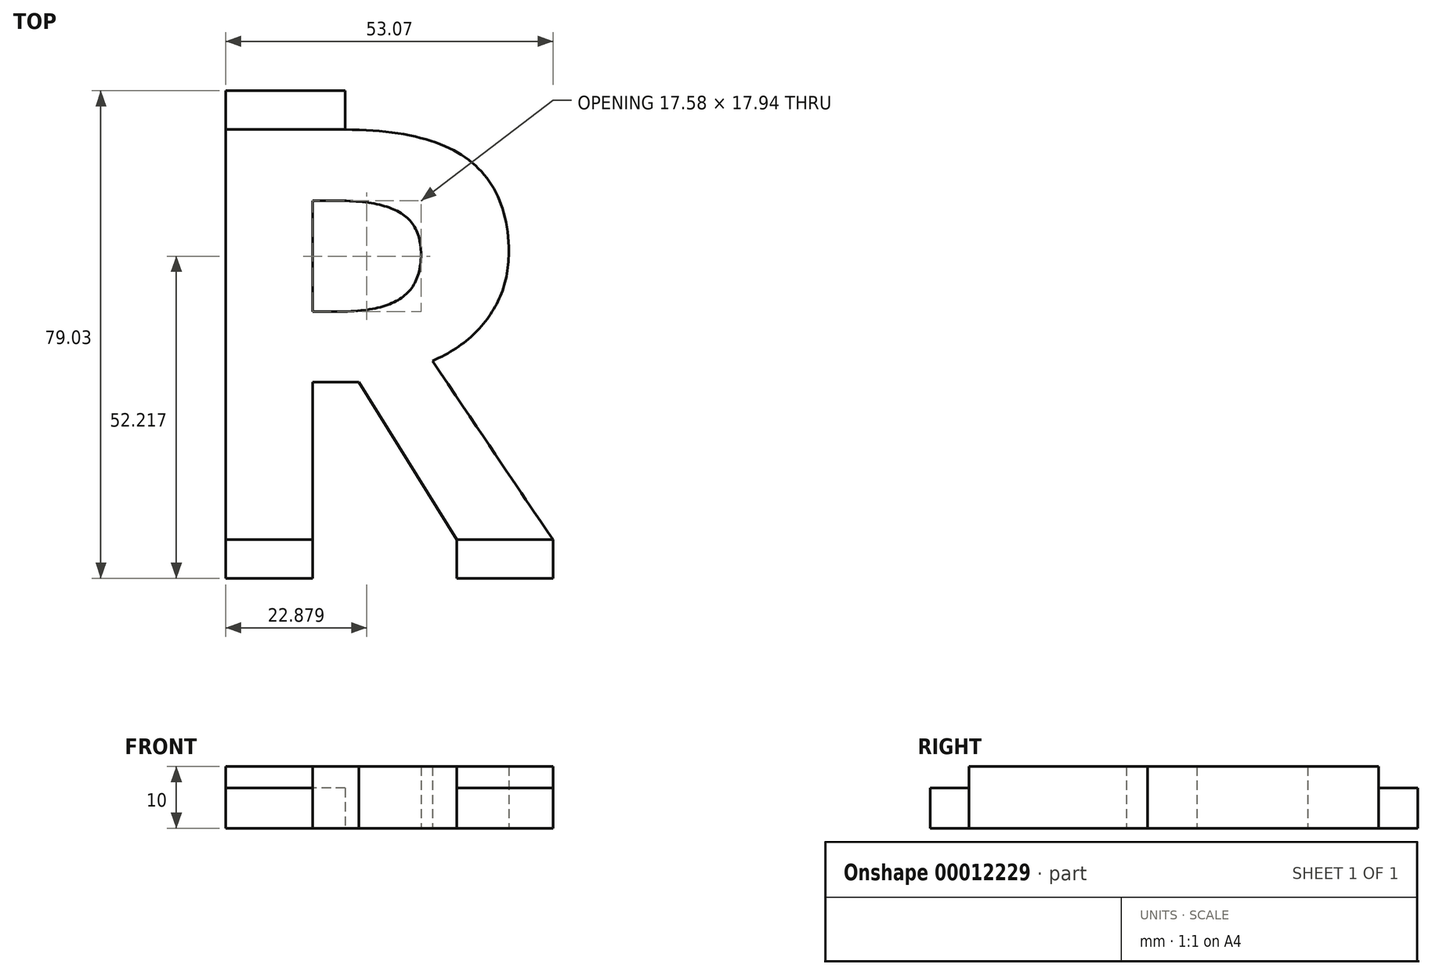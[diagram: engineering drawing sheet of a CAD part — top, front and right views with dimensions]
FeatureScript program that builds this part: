
annotation { "Feature Type Name" : "Feature", "Feature Type Description" : "" }
export const myFeature = defineFeature(function(context is Context, id is Id, definition is map)
    precondition{}
    {
        {
            var Q0;
            Q0=qCreatedBy(makeId("Top.planeOp"),FACE);
            var sketch = newSketch(context, id + "F0", { "sketchPlane" : qUnion([Q0])});
            skText(sketch, "E0", { "text": "R", "fontName": "OpenSans-Bold.ttf"});
            skLineSegment(sketch, "E1", {"start": v(-53.06, 66.47) * mm, "end": v(-5.63, 66.47) * mm, "construction": true});
            const initialGuessF0  = {"E0": [-0.06143, 0, 1, 0, 0.067]};
            skSetInitialGuess(sketch, initialGuessF0);
            skSolve(sketch);
        }
        {
            var Q0;
            Q0=makeQuery(id+"F0.imprint","IMPRINT",FACE,{"disambiguationData":[TD([[makeQuery(id+"F0.imprint","IMPRINT",EDGE,{"derivedFrom":sQuery(id+"F0.wireOp",EDGE,"E0.sketch_text.stroke-0")}),-1.0]])]});
            extrude(context, id + "F1", {"entities" : qUnion([Q0]), "depth" : 10 * mm});
        }
        {
            var Q0;
            Q0=makeQuery(id+"F1.opExtrude","SWEPT_FACE",FACE,{"disambiguationData":[OSD([sQuery(id+"F0.wireOp",EDGE,"E0.sketch_text.stroke-8")])]});
            var sketch = newSketch(context, id + "F2", { "sketchPlane" : qUnion([Q0])});
            skLineSegment(sketch, "E2.0.0", {"start": v(-53.07, 0) * mm, "end": v(-38.98, 0) * mm});
            skLineSegment(sketch, "E2.0.1", {"start": v(-38.98, 0) * mm, "end": v(-38.98, 10) * mm});
            skLineSegment(sketch, "E2.0.2", {"start": v(-38.98, 10) * mm, "end": v(-53.07, 10) * mm});
            skLineSegment(sketch, "E2.0.3", {"start": v(-53.07, 10) * mm, "end": v(-53.07, 0) * mm});
            skLineSegment(sketch, "E3.0.0", {"start": v(-15.63, 0) * mm, "end": v(0, 0) * mm});
            skLineSegment(sketch, "E3.0.1", {"start": v(0, 0) * mm, "end": v(0, 10) * mm});
            skLineSegment(sketch, "E3.0.2", {"start": v(0, 10) * mm, "end": v(-15.63, 10) * mm});
            skLineSegment(sketch, "E3.0.3", {"start": v(-15.63, 10) * mm, "end": v(-15.63, 0) * mm});
            skLineSegment(sketch, "E4.top", {"start": v(-53.07, 6.5) * mm, "end": v(-38.98, 6.5) * mm});
            skLineSegment(sketch, "E4.left", {"start": v(-53.07, 0) * mm, "end": v(-53.07, 6.5) * mm});
            skLineSegment(sketch, "E4.right", {"start": v(-38.98, 0) * mm, "end": v(-38.98, 6.5) * mm});
            skLineSegment(sketch, "E5.top", {"start": v(-15.63, 6.5) * mm, "end": v(0, 6.5) * mm});
            skLineSegment(sketch, "E5.left", {"start": v(-15.63, 0) * mm, "end": v(-15.63, 6.5) * mm});
            skLineSegment(sketch, "E5.right", {"start": v(0, 0) * mm, "end": v(0, 6.5) * mm});
            skSolve(sketch);
        }
        {
            var Q0;
            Q0=makeQuery(id+"F2.imprint","IMPRINT",FACE,{"disambiguationData":[TD([[makeQuery(id+"F2.imprint","IMPRINT",EDGE,{"derivedFrom":sQuery(id+"F2.wireOp",EDGE,"E2.0.0")}),-1.0]])]});
            var Q1;
            Q1=makeQuery(id+"F2.imprint","IMPRINT",FACE,{"disambiguationData":[TD([[makeQuery(id+"F2.imprint","IMPRINT",EDGE,{"derivedFrom":sQuery(id+"F2.wireOp",EDGE,"E3.0.0")}),1.0]])]});
            extrude(context, id + "F3", {"entities" : qUnion([Q0, Q1]), "operationType" : NewBodyOperationType.ADD, "depth" : 6.3 * mm});
        }
        {
            var Q0;
            Q0=makeQuery(id+"F1.opExtrude","SWEPT_FACE",FACE,{"disambiguationData":[OSD([sQuery(id+"F0.wireOp",EDGE,"E0.sketch_text.stroke-10")])]});
            var sketch = newSketch(context, id + "F4", { "sketchPlane" : qUnion([Q0])});
            skLineSegment(sketch, "E6.0.0", {"start": v(33.72, 0) * mm, "end": v(53.07, 0) * mm});
            skLineSegment(sketch, "E6.0.1", {"start": v(53.07, 0) * mm, "end": v(53.07, 10) * mm});
            skLineSegment(sketch, "E6.0.2", {"start": v(53.07, 10) * mm, "end": v(33.72, 10) * mm});
            skLineSegment(sketch, "E6.0.3", {"start": v(33.72, 10) * mm, "end": v(33.72, 0) * mm});
            skLineSegment(sketch, "E7.top", {"start": v(33.72, 6.5) * mm, "end": v(53.07, 6.5) * mm});
            skLineSegment(sketch, "E7.left", {"start": v(33.72, 0) * mm, "end": v(33.72, 6.5) * mm});
            skLineSegment(sketch, "E7.right", {"start": v(53.07, 0) * mm, "end": v(53.07, 6.5) * mm});
            skSolve(sketch);
        }
        {
            var Q0;
            Q0=makeQuery(id+"F4.imprint","IMPRINT",FACE,{"disambiguationData":[TD([[makeQuery(id+"F4.imprint","IMPRINT",EDGE,{"derivedFrom":sQuery(id+"F4.wireOp",EDGE,"E6.0.0")}),-1.0]])]});
            extrude(context, id + "F5", {"entities" : qUnion([Q0]), "operationType" : NewBodyOperationType.ADD, "depth" : 6.3 * mm});
        }
    });
